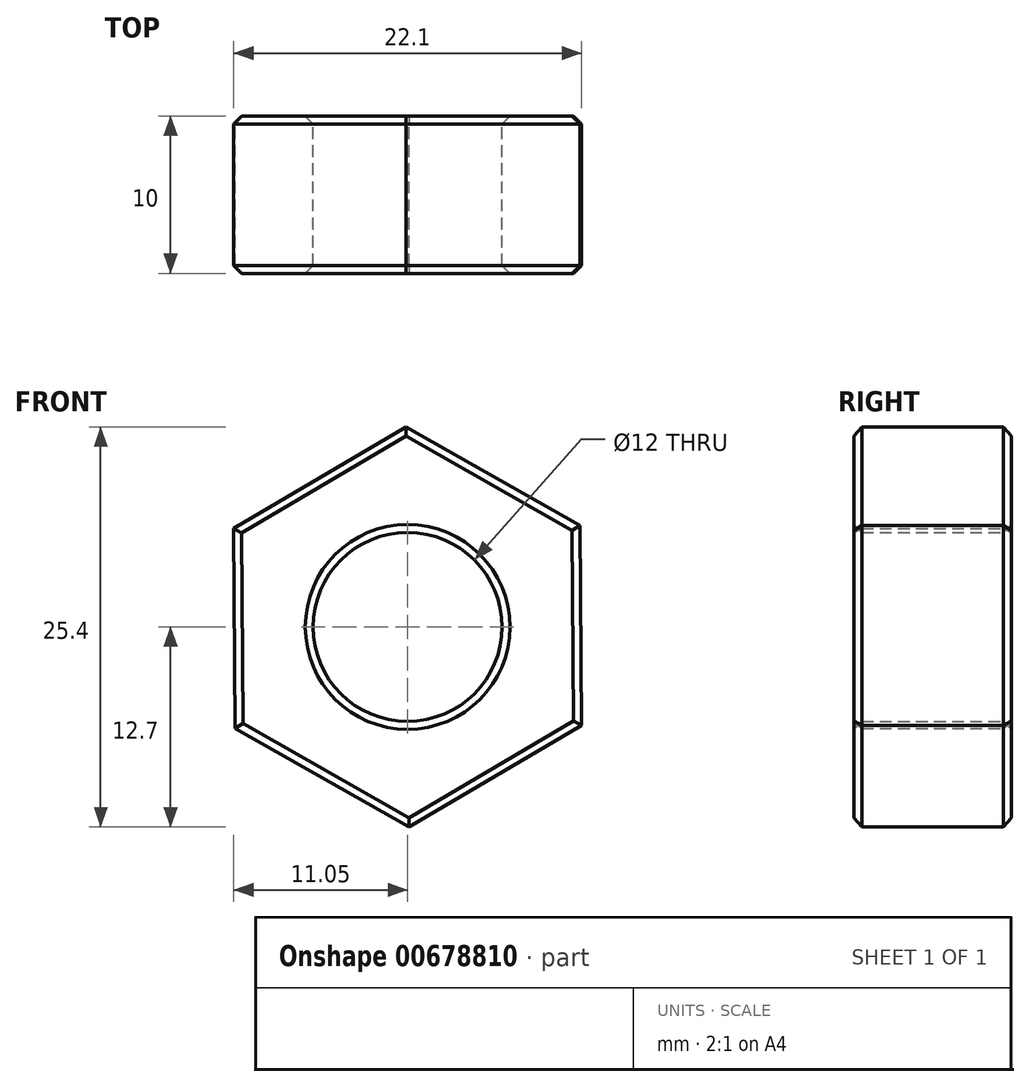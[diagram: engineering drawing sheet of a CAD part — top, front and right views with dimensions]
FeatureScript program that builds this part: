
annotation { "Feature Type Name" : "Feature", "Feature Type Description" : "" }
export const myFeature = defineFeature(function(context is Context, id is Id, definition is map)
    precondition{}
    {
        {
            var Q0;
            Q0=qCreatedBy(makeId("Front.planeOp"),FACE);
            var sketch = newSketch(context, id + "F0", { "sketchPlane" : qUnion([Q0])});
            skCircle(sketch, "E0.cCircle", {"center": v(0, 0) * mm, "radius": 11 * mm, "construction": true});
            skLineSegment(sketch, "E0.0", {"start": v(-11.05, 6.27) * mm, "end": v(-0.1, 12.7) * mm});
            skLineSegment(sketch, "E0.1", {"start": v(-0.1, 12.7) * mm, "end": v(10.95, 6.43) * mm});
            skLineSegment(sketch, "E0.2", {"start": v(10.95, 6.43) * mm, "end": v(11.05, -6.27) * mm});
            skLineSegment(sketch, "E0.3", {"start": v(11.05, -6.27) * mm, "end": v(0.1, -12.7) * mm});
            skLineSegment(sketch, "E0.4", {"start": v(0.1, -12.7) * mm, "end": v(-10.95, -6.43) * mm});
            skLineSegment(sketch, "E0.5", {"start": v(-10.95, -6.43) * mm, "end": v(-11.05, 6.27) * mm});
            skPoint(sketch, "E0.0.midPoint", {"position": v(-5.57, 9.48) * mm});
            skCircle(sketch, "E1", {"center": v(0, 0) * mm, "radius": 6 * mm});
            skSolve(sketch);
        }
        {
            var Q0;
            Q0=makeQuery(id+"F0.imprint","IMPRINT",FACE,{"disambiguationData":[TD([[makeQuery(id+"F0.imprint","IMPRINT",EDGE,{"derivedFrom":sQuery(id+"F0.wireOp",EDGE,"E0.0")}),-1.0]])]});
            extrude(context, id + "F1", {"entities" : qUnion([Q0]), "depth" : 10 * mm, "offsetDistance" : 25 * mm});
        }
        {
            var Q0;
            Q0=makeQuery(id+"F1.opExtrude","CAP_EDGE",EDGE,{"disambiguationData":[OSD([sQuery(id+"F0.wireOp",EDGE,"E0.1")])],"isStart":true});
            var Q1;
            Q1=makeQuery(id+"F1.opExtrude","CAP_EDGE",EDGE,{"disambiguationData":[OSD([sQuery(id+"F0.wireOp",EDGE,"E0.0")])],"isStart":true});
            var Q2;
            Q2=makeQuery(id+"F1.opExtrude","CAP_EDGE",EDGE,{"disambiguationData":[OSD([sQuery(id+"F0.wireOp",EDGE,"E0.5")])],"isStart":true});
            var Q3;
            Q3=makeQuery(id+"F1.opExtrude","CAP_EDGE",EDGE,{"disambiguationData":[OSD([sQuery(id+"F0.wireOp",EDGE,"E0.4")])],"isStart":true});
            var Q4;
            Q4=makeQuery(id+"F1.opExtrude","CAP_EDGE",EDGE,{"disambiguationData":[OSD([sQuery(id+"F0.wireOp",EDGE,"E0.3")])],"isStart":true});
            var Q5;
            Q5=makeQuery(id+"F1.opExtrude","CAP_EDGE",EDGE,{"disambiguationData":[OSD([sQuery(id+"F0.wireOp",EDGE,"E0.2")])],"isStart":true});
            var Q6;
            Q6=makeQuery(id+"F1.opExtrude","CAP_EDGE",EDGE,{"disambiguationData":[OSD([sQuery(id+"F0.wireOp",EDGE,"E0.1")])],"isStart":false});
            var Q7;
            Q7=makeQuery(id+"F1.opExtrude","CAP_EDGE",EDGE,{"disambiguationData":[OSD([sQuery(id+"F0.wireOp",EDGE,"E0.0")])],"isStart":false});
            var Q8;
            Q8=makeQuery(id+"F1.opExtrude","CAP_EDGE",EDGE,{"disambiguationData":[OSD([sQuery(id+"F0.wireOp",EDGE,"E0.5")])],"isStart":false});
            var Q9;
            Q9=makeQuery(id+"F1.opExtrude","CAP_EDGE",EDGE,{"disambiguationData":[OSD([sQuery(id+"F0.wireOp",EDGE,"E0.4")])],"isStart":false});
            var Q10;
            Q10=makeQuery(id+"F1.opExtrude","CAP_EDGE",EDGE,{"disambiguationData":[OSD([sQuery(id+"F0.wireOp",EDGE,"E0.3")])],"isStart":false});
            var Q11;
            Q11=makeQuery(id+"F1.opExtrude","CAP_EDGE",EDGE,{"disambiguationData":[OSD([sQuery(id+"F0.wireOp",EDGE,"E0.2")])],"isStart":false});
            var Q12;
            Q12=makeQuery(id+"F1.opExtrude","CAP_EDGE",EDGE,{"disambiguationData":[OSD([sQuery(id+"F0.wireOp",EDGE,"E1")])],"isStart":false});
            var Q13;
            Q13=makeQuery(id+"F1.opExtrude","CAP_EDGE",EDGE,{"disambiguationData":[OSD([sQuery(id+"F0.wireOp",EDGE,"E1")])],"isStart":true});
            chamfer(context, id + "F2", {"entities" : qUnion([Q0, Q1, Q2, Q3, Q4, Q5, Q6, Q7, Q8, Q9, Q10, Q11, Q12, Q13]), "width" : 0.5 * mm, "tangentPropagation" : true});
        }
    });
